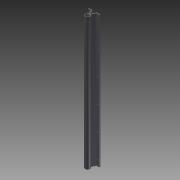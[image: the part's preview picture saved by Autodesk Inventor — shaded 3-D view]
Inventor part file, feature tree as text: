
AUTODESK INVENTOR PART (.ipt)
format: ipt  version: 2013 (Build 170138000, 138)  size: 158,208 bytes
history: native  units: in
note: dims shown in document units (in); Inventor stores cm internally (conversion verified against a paired STEP export)
features: sketch x2, imported_body x1
ambient origin geometry x8: Origin, YZ Plane, XZ Plane, XY Plane, X Axis, Y Axis, Z Axis, Center Point
feature tree (3):
  sketch  "Sketch4"
  sketch  "Sketch5"
  imported_body  "Base1"
